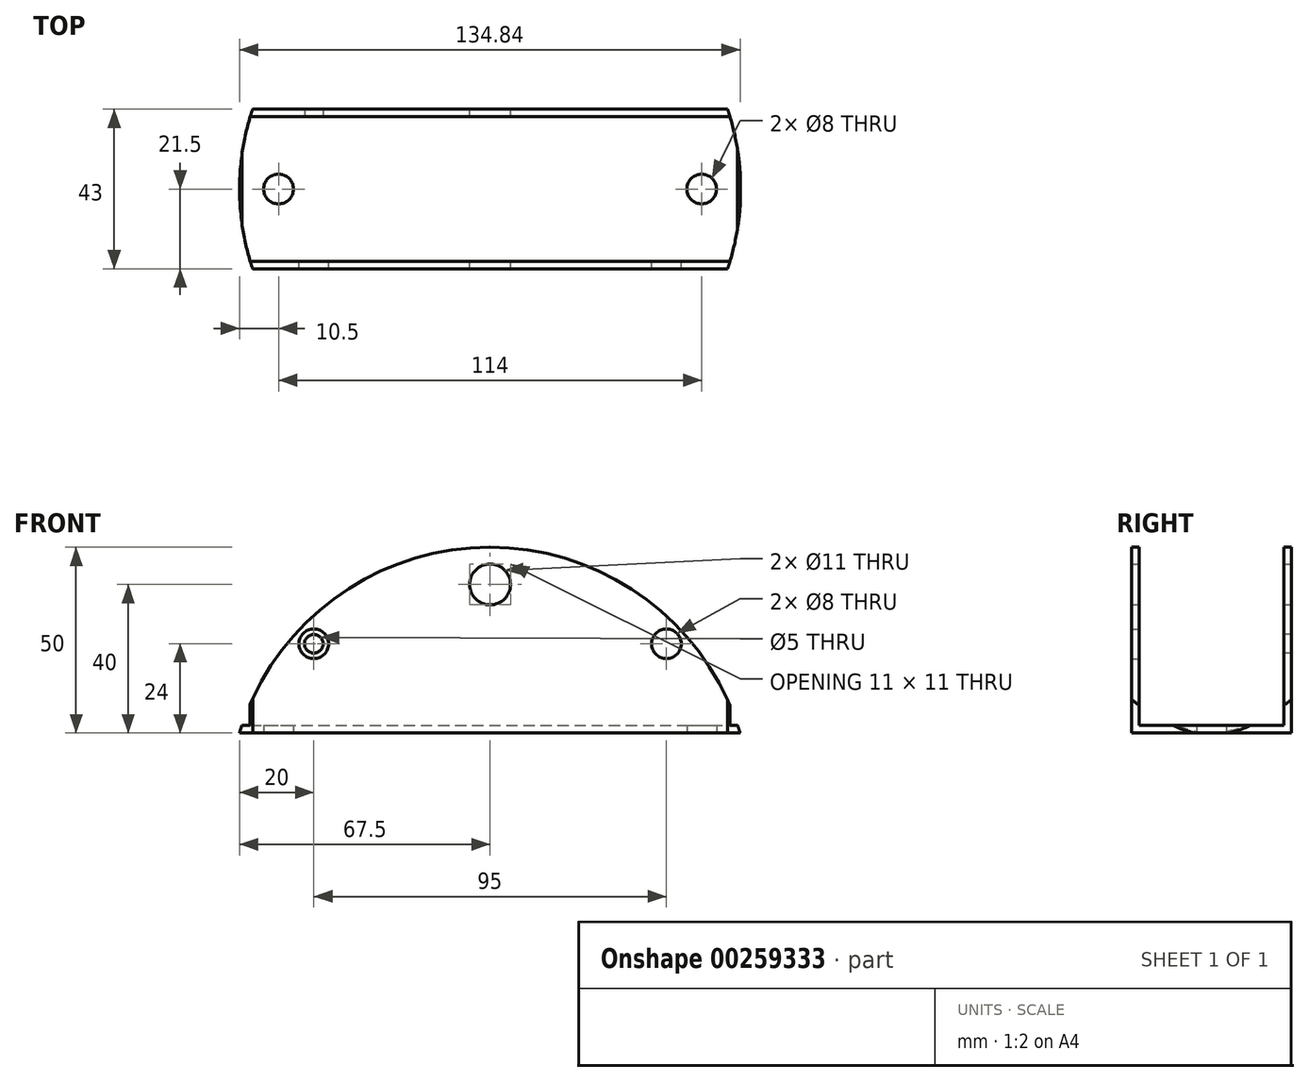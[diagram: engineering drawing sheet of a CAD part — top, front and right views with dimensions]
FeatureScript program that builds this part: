
annotation { "Feature Type Name" : "Feature", "Feature Type Description" : "" }
export const myFeature = defineFeature(function(context is Context, id is Id, definition is map)
    precondition{}
    {
        {
            var Q0;
            Q0=qCreatedBy(makeId("Top.planeOp"),FACE);
            var sketch = newSketch(context, id + "F0", { "sketchPlane" : qUnion([Q0])});
            skArc(sketch, "E0", {"start": v(63.98, -21.5) * mm, "mid": v(67.5, 0) * mm, "end": v(63.98, 21.5) * mm});
            skLineSegment(sketch, "E1.top", {"start": v(-63.98, -21.5) * mm, "end": v(0, -21.5) * mm});
            skLineSegment(sketch, "E2.MirrorCS", {"start": v(-63.98, 21.5) * mm, "end": v(0, 21.5) * mm});
            skLineSegment(sketch, "E3.MirrorCS", {"start": v(63.98, 21.5) * mm, "end": v(0, 21.5) * mm});
            skLineSegment(sketch, "E4.MirrorCS", {"start": v(63.98, -21.5) * mm, "end": v(0, -21.5) * mm});
            skArc(sketch, "E5.MirrorC", {"start": v(63.98, 21.5) * mm, "mid": v(67.5, 0) * mm, "end": v(63.98, -21.5) * mm});
            skPoint(sketch, "E6.orphan", {"position": v(67.5, 21.5) * mm});
            skPoint(sketch, "E7.orphan", {"position": v(67.5, -21.5) * mm});
            skPoint(sketch, "E1.left.end.orphan", {"position": v(-67.5, -21.5) * mm});
            skPoint(sketch, "E8.orphan", {"position": v(-67.5, 21.5) * mm});
            skArc(sketch, "E9.trimOffspring", {"start": v(-63.98, -21.5) * mm, "mid": v(-67.5, 0) * mm, "end": v(-63.98, 21.5) * mm});
            skArc(sketch, "E10.trimOffspring", {"start": v(-63.98, 21.5) * mm, "mid": v(-67.5, 0) * mm, "end": v(-63.98, -21.5) * mm});
            skLineSegment(sketch, "E11", {"start": v(-67.5, 0) * mm, "end": v(0, 0) * mm, "construction": true});
            skLineSegment(sketch, "E12", {"start": v(0, 21.5) * mm, "end": v(0, -21.5) * mm, "construction": true});
            skLineSegment(sketch, "E13.MirrorCS", {"start": v(67.5, 0) * mm, "end": v(0, 0) * mm, "construction": true});
            skSolve(sketch);
        }
        {
            var Q0;
            Q0=makeQuery(id+"F0.imprint","IMPRINT",FACE,{"disambiguationData":[TD([[makeQuery(id+"F0.imprint","IMPRINT",EDGE,{"derivedFrom":sQuery(id+"F0.wireOp",EDGE,"E1.top")}),1.0]])]});
            extrude(context, id + "F1", {"entities" : qUnion([Q0]), "depth" : 50 * mm});
        }
        {
            var Q0;
            Q0=qCreatedBy(makeId("Front.planeOp"),FACE);
            var sketch = newSketch(context, id + "F2", { "sketchPlane" : qUnion([Q0])});
            skLineSegment(sketch, "E14", {"start": v(0, 0) * mm, "end": v(0, 50) * mm, "construction": true});
            skArc(sketch, "E15", {"start": v(67.34, 0) * mm, "mid": v(-0.1, 50) * mm, "end": v(-67.52, 0) * mm});
            skLineSegment(sketch, "E16", {"start": v(-67.52, 0) * mm, "end": v(67.34, 0) * mm});
            skCircle(sketch, "E17", {"center": v(0, 40) * mm, "radius": 5.5 * mm});
            skSolve(sketch);
        }
        {
            var Q0;
            Q0 = qSketchRegion(id + "F2", true);
            extrude(context, id + "F3", {"entities" : qUnion([Q0]), "endBound" : BoundingType.SYMMETRIC, "depth" : 45 * mm});
        }
        {
            var Q0;
            Q0=makeQuery(id+"F1.opExtrude","SWEPT_BODY",BODY,{"disambiguationData":[OSD([sQuery(id+"F0.wireOp",EDGE,"E1.top"),sQuery(id+"F0.wireOp",EDGE,"E2.MirrorCS"),sQuery(id+"F0.wireOp",EDGE,"E3.MirrorCS"),sQuery(id+"F0.wireOp",EDGE,"E4.MirrorCS"),sQuery(id+"F0.wireOp",EDGE,"E5.MirrorC"),sQuery(id+"F0.wireOp",EDGE,"E10.trimOffspring")])]});
            var Q1;
            Q1=makeQuery(id+"F3.opExtrude","SWEPT_BODY",BODY,{"disambiguationData":[OSD([sQuery(id+"F2.wireOp",EDGE,"E15"),sQuery(id+"F2.wireOp",EDGE,"E16")])]});
            booleanBodies(context, id + "F4", {"operationType" : BooleanOperationType.INTERSECTION, "tools" : qUnion([Q0, Q1])});
        }
        {
            var Q0;
            Q0=qCreatedBy(makeId("Right.planeOp"),FACE);
            var sketch = newSketch(context, id + "F5", { "sketchPlane" : qUnion([Q0])});
            skCircle(sketch, "E18", {"center": v(-22.5, 0) * mm, "radius": 3 * mm, "construction": true});
            skLineSegment(sketch, "E19", {"start": v(-19.5, 0) * mm, "end": v(-19.5, 2) * mm});
            skLineSegment(sketch, "E20", {"start": v(-19.5, 2) * mm, "end": v(-19.5, 52) * mm, "construction": true});
            skLineSegment(sketch, "E21.right", {"start": v(-19.5, 2) * mm, "end": v(-19.5, 52) * mm});
            skLineSegment(sketch, "E22", {"start": v(0, 2) * mm, "end": v(0, 52) * mm});
            skLineSegment(sketch, "E23", {"start": v(0, 52) * mm, "end": v(-19.5, 52) * mm});
            skLineSegment(sketch, "E24", {"start": v(-19.5, 2) * mm, "end": v(0, 2) * mm});
            skLineSegment(sketch, "E25.MirrorCS", {"start": v(0, 52) * mm, "end": v(19.5, 52) * mm});
            skLineSegment(sketch, "E26.MirrorCS", {"start": v(19.5, 2) * mm, "end": v(19.5, 52) * mm});
            skLineSegment(sketch, "E27.MirrorCS", {"start": v(19.5, 2) * mm, "end": v(0, 2) * mm});
            skSolve(sketch);
        }
        {
            var Q0;
            Q0 = qSketchRegion(id + "F5", true);
            extrude(context, id + "F6", {"entities" : qUnion([Q0]), "operationType" : NewBodyOperationType.REMOVE, "endBound" : BoundingType.SYMMETRIC, "oppositeDirection" : true, "depth" : 180 * mm});
        }
        {
            var Q0;
            Q0=qCreatedBy(makeId("Top.planeOp"),FACE);
            var sketch = newSketch(context, id + "F7", { "sketchPlane" : qUnion([Q0])});
            skCircle(sketch, "E28", {"center": v(57, 0) * mm, "radius": 4 * mm});
            skCircle(sketch, "E29.MirrorC", {"center": v(-57, 0) * mm, "radius": 4 * mm});
            skSolve(sketch);
        }
        {
            var Q0;
            Q0 = qSketchRegion(id + "F7", true);
            extrude(context, id + "F8", {"entities" : qUnion([Q0]), "operationType" : NewBodyOperationType.REMOVE, "endBound" : BoundingType.THROUGH_ALL, "depth" : 25 * mm});
        }
        {
            var Q0;
            Q0=qCreatedBy(makeId("Front.planeOp"),FACE);
            var sketch = newSketch(context, id + "F9", { "sketchPlane" : qUnion([Q0])});
            skLineSegment(sketch, "E30", {"start": v(0, 0) * mm, "end": v(0, -24) * mm});
            skCircle(sketch, "E31.MirrorC", {"center": v(47.5, 24) * mm, "radius": 2.5 * mm});
            skCircle(sketch, "E32.MirrorC", {"center": v(-47.5, 24) * mm, "radius": 2.5 * mm});
            skSolve(sketch);
        }
        {
            var Q0;
            Q0=makeQuery(id+"F9.imprint","IMPRINT",FACE,{"disambiguationData":[TD([[makeQuery(id+"F9.imprint","IMPRINT",EDGE,{"derivedFrom":sQuery(id+"F9.wireOp",EDGE,"E32.MirrorC")}),1.0]])]});
            var Q1;
            Q1=makeQuery(id+"F9.imprint","IMPRINT",FACE,{"disambiguationData":[TD([[makeQuery(id+"F9.imprint","IMPRINT",EDGE,{"derivedFrom":sQuery(id+"F9.wireOp",EDGE,"E31.MirrorC")}),-1.0]])]});
            var Q2;
            Q2=sQuery(id+"F9.wireOp",EDGE,"E31.MirrorC");
            extrude(context, id + "F10", {"entities" : qUnion([Q0, Q1]), "operationType" : NewBodyOperationType.REMOVE, "surfaceEntities" : qUnion([Q2]), "oppositeDirection" : true, "depth" : 50 * mm});
        }
        {
            var Q0;
            Q0=qCreatedBy(makeId("Front.planeOp"),FACE);
            var sketch = newSketch(context, id + "F11", { "sketchPlane" : qUnion([Q0])});
            skCircle(sketch, "E33.MirrorC", {"center": v(47.5, 24) * mm, "radius": 4 * mm});
            skCircle(sketch, "E34.MirrorC", {"center": v(-47.5, 24) * mm, "radius": 4 * mm});
            skSolve(sketch);
        }
        {
            var Q0;
            Q0 = qSketchRegion(id + "F11", true);
            extrude(context, id + "F12", {"entities" : qUnion([Q0]), "operationType" : NewBodyOperationType.REMOVE, "depth" : 40 * mm});
        }
    });
